# Revit family: crometta_1jet_green_shower_set_0_65_m_26554400
name_source: partatom
category: Plumbing Fixtures
revit_build: Autodesk Revit 2015 (Build: 20140903_1530(x64)
units: mm (PartAtom-declared; Revit-internal decimal feet)

## types (1)
- white/chrome
    BIMobject category = Showers
    BOSUseNativeGeometries = 1
    Brand url = http://www.hansgrohe-int.com
    Default Elevation = 4' - 0"
    Design country = Germany
    EAN code = https://4011097791968
    Edition number = 1
    IFC Classification = Sanitary Terminal
    Installation instructions = https://pro.hansgrohe-int.com
    Manufacturer country = Germany
    Manufacturer name = hansgrohe
    Masterformat 2014 Code = 01 52 19
    Masterformat 2014 Description = Sanitary Facilities
    NBS Reference Code = 31-76
    NBS Reference Description = Sanitary Dispensing And Disposal Units
    Nominal height = 0
    Nominal width = 0
    OmniClass Code = 23-19 31 17
    OmniClass Description = Sanitary Room Units
    Product Guid = a427cba4-0f37-48bf-98f2-e26fbcae9803
    Product SKU = 26554400
    Product data url = https://bimobject.com
    Product family = Crometta
    Product group = Wallbar sets
    Product name = Crometta 1jet Green shower set 0.65 m  26554400
    Product url = https://pro.hansgrohe-int.com
    QR code = http://bimobject.com
    Technical description = https://pro.hansgrohe-int.com
    UNSPSC Code = 301815
    Uniclass 1.4 Code = L721
    Uniclass 1.4 Description = Sanitary equipment
    Uniclass 2.0 Code = PR-31-76
    Uniclass 2.0 Description = Sanitary Dispensing And Disposal Units
    Uniclass 2015 Code = Pr_40_20
    Uniclass 2015 Name = Sanitary fittings and accessories
    Uniformat II Code = D2010
    Uniformat II Description = Plumbing Fixtures
    Weight Net (Kg) = 0

## geometry (parser evidence)
native form markers: Sweep x2
no freeform markers — native parametric forms only
